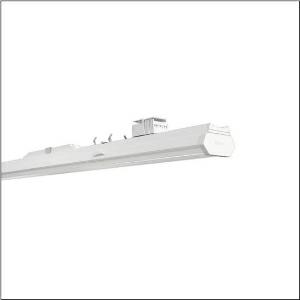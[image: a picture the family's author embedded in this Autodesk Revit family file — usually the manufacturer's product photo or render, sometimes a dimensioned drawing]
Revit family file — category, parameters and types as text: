
# Revit family: licross_21_protected_mo_52tp127n38xg
name_source: partatom
category: Lighting Fixtures
units: mm (PartAtom-declared; Revit-internal decimal feet)

## family parameters
Cut with Voids When Loaded = No
Host = Face
Light Source = No
Part Type = Normal
Room Calculation Point = No
Round Connector Dimension = Use Diameter
Shared = No

## types (1)
- Licross 21 Protected MO (1 x LED, 8080 lm, 47.9 W, 3000K)
    Apparent Load = 48 VA
    CIE Flux Codes = 73 92 98 99 100
    Color Rendering = 80
    Color Temperature = 3000K
    Default Elevation = 1800 mm
    Description = Licross 21 Protected MO, luminaire insert, of sheet steel, galvanised, coil coated, white, length: 1.500mm, width: 90mm, height: 101mm, LED rated luminous flux: 8.080lm, light colour: 830, SDCM (Standard Deviation of Colour Matching)MacAdam ≤ 3 SDCM (initial), control gear: ON/OFF, with plug, 3-pole, with phase selection, mains connection: 220..240V, AC, 50/60Hz, rated input power: 48W, internal wiring halogen-free, primary light control with lens, of plastic, primary optical cover: cover, of PMMA, light emission: direct distribution, primary light characteristic: symmetric, protection rating (complete): IP64, insulation class (complete): insulation class I (protective earthing), certification: CE, ENEC, VDE, UKCA, protection symbol: D if used in an environment with conductive dust loads with corresponding accessories, impact resistance: IK06, permissible ambient temperature for indoor applications: -35..+45°C, corresponds to IFS (International Featured Standards) requirements for safety and quality in the food industry, reducing of maximum allowable ambient temperature of 5°C with ceiling mounting, LABS conformity tested according to VDMA 24364:2018-05, The light source and the operating device comply with the requirements of the Ecodesign Regulation (EU) 2019/2020 and are replaceable in accordance with this regulation, packaging unit: 1 piece
    Height = 92 mm
    Lamp = 1 x LED
    Lamp Light Flux = 8080 lm
    Lamp Power = 47.9 W
    Lamp count = 1
    Length = 1500 mm
    Luminous efficacy = 169 lm/W
    Manufacturer = Siteco
    ModVariant = No
    Model = 52TP127N38XG
    Mounting Place = Ceiling
    Mounting Type = Pendant
    Number of Poles = 1
    OnlyDefault = Yes
    Power Factor = 1
    Product Name = Licross 21 Protected MO
    Product group = luminaire insert | ceiling pendant
    ProductGroupID = 901
    Protection Class = Protection class I
    Protection Degree = IP 64
    RLX_Detail_Level = 1
    RLX_Emergency_Light_Flux = 0 lm
    RLX_Emergency_Type = 0
    RLX_Emergency_Type_DB = No
    RlxData = <blob elided: 20949 chars, md5=bd01322c>
    Socket = socket
    Standby Power = 0 W
    System Light Flux = 8080 lm
    System Power = 48 W
    Type Comments = Product without accessories
    Type Image = l_1256148.jpg
    URL = http://relux.com
    VarID = ---
    Voltage = 0 V
    Weight = 0.00 kg
    Width = 88 mm

## geometry (parser evidence)
native form markers: Blend x4, Sweep x10
no freeform markers — native parametric forms only
